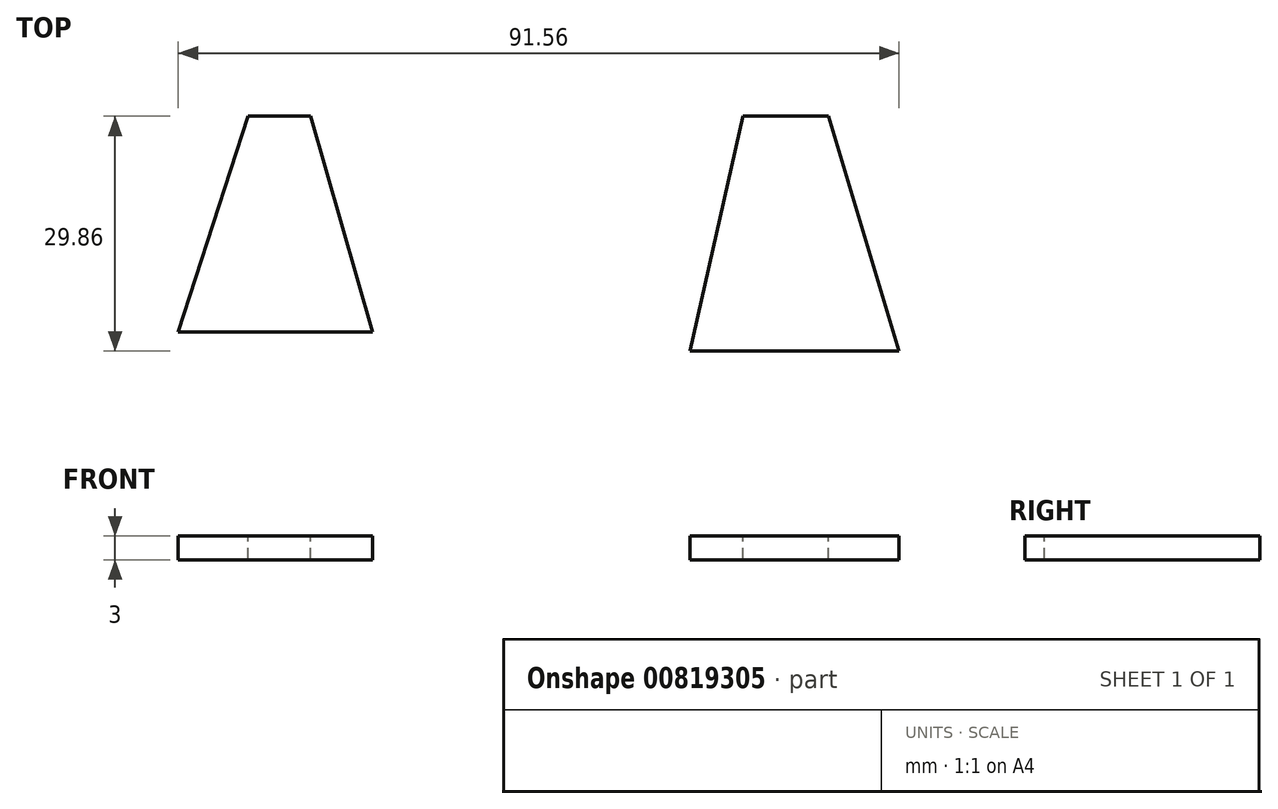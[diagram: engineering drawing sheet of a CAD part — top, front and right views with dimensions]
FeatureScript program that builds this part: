
annotation { "Feature Type Name" : "Feature", "Feature Type Description" : "" }
export const myFeature = defineFeature(function(context is Context, id is Id, definition is map)
    precondition{}
    {
        {
            var Q0;
            Q0=qCreatedBy(makeId("Top.planeOp"),FACE);
            var sketch = newSketch(context, id + "F0", { "sketchPlane" : qUnion([Q0])});
            skLineSegment(sketch, "E0.bottom", {"start": v(0, 0) * mm, "end": v(100, 0) * mm});
            skLineSegment(sketch, "E0.top", {"start": v(0, 150) * mm, "end": v(100, 150) * mm});
            skLineSegment(sketch, "E0.left", {"start": v(0, 0) * mm, "end": v(0, 150) * mm});
            skLineSegment(sketch, "E0.right", {"start": v(100, 0) * mm, "end": v(100, 150) * mm});
            skSolve(sketch);
        }
        {
            var Q0;
            Q0=makeQuery(id+"F0.imprint","IMPRINT",FACE,{"disambiguationData":[TD([[makeQuery(id+"F0.imprint","IMPRINT",EDGE,{"derivedFrom":sQuery(id+"F0.wireOp",EDGE,"E0.bottom")}),1.0]])]});
            var sketch = newSketch(context, id + "F1", { "sketchPlane" : qUnion([Q0])});
            skSolve(sketch);
        }
        {
            var Q0;
            Q0=makeQuery(id+"F1.imprint","IMPRINT",FACE,{"disambiguationData":[TD([[makeQuery(id+"F1.imprint","IMPRINT",EDGE,{"derivedFrom":makeQuery(id+"F0.imprint","IMPRINT",EDGE,{"derivedFrom":sQuery(id+"F0.wireOp",EDGE,"E0.bottom")})}),1.0]])]});
            extrude(context, id + "F2", {"entities" : qUnion([Q0]), "depth" : 3 * mm, "offsetDistance" : 25 * mm});
        }
        {
            var Q0;
            Q0=makeQuery(id+"F2.opExtrude","CAP_FACE",FACE,{"disambiguationData":[OSD([sQuery(id+"F0.wireOp",EDGE,"E0.bottom"),sQuery(id+"F0.wireOp",EDGE,"E0.top"),sQuery(id+"F0.wireOp",EDGE,"E0.left"),sQuery(id+"F0.wireOp",EDGE,"E0.right")])],"isStart":false});
            var sketch = newSketch(context, id + "F3", { "sketchPlane" : qUnion([Q0])});
            skLineSegment(sketch, "E1", {"start": v(0, 150) * mm, "end": v(100, 150) * mm});
            skLineSegment(sketch, "E2", {"start": v(100, 150) * mm, "end": v(38.52, 247.5) * mm});
            skLineSegment(sketch, "E3", {"start": v(38.52, 247.5) * mm, "end": v(0, 150) * mm});
            skSolve(sketch);
        }
        {
            var Q0;
            Q0=makeQuery(id+"F3.imprint","IMPRINT",FACE,{"disambiguationData":[TD([[makeQuery(id+"F3.imprint","IMPRINT",EDGE,{"derivedFrom":sQuery(id+"F3.wireOp",EDGE,"E1")}),1.0]])]});
            extrude(context, id + "F4", {"entities" : qUnion([Q0]), "operationType" : NewBodyOperationType.ADD, "oppositeDirection" : true, "depth" : 3 * mm, "offsetDistance" : 25 * mm});
        }
        {
            var Q0;
            Q0=makeQuery(id+"F4.boolean.opBoolean","MERGE",FACE,{"derivedFrom":[makeQuery(id+"F2.opExtrude","CAP_FACE",FACE,{"disambiguationData":[OSD([sQuery(id+"F0.wireOp",EDGE,"E0.bottom"),sQuery(id+"F0.wireOp",EDGE,"E0.top"),sQuery(id+"F0.wireOp",EDGE,"E0.left"),sQuery(id+"F0.wireOp",EDGE,"E0.right")])],"isStart":false}),makeQuery(id+"F4.opExtrude","CAP_FACE",FACE,{"disambiguationData":[OSD([sQuery(id+"F3.wireOp",EDGE,"E1"),sQuery(id+"F3.wireOp",EDGE,"E2"),sQuery(id+"F3.wireOp",EDGE,"E3")])],"isStart":true})]});
            var sketch = newSketch(context, id + "F5", { "sketchPlane" : qUnion([Q0])});
            skLineSegment(sketch, "E4", {"start": v(8.85, 0) * mm, "end": v(0, -27.4) * mm});
            skLineSegment(sketch, "E5", {"start": v(0, -27.4) * mm, "end": v(24.68, -27.4) * mm});
            skLineSegment(sketch, "E6", {"start": v(24.68, -27.4) * mm, "end": v(16.82, 0) * mm});
            skLineSegment(sketch, "E7", {"start": v(16.82, 0) * mm, "end": v(71.74, 0) * mm});
            skLineSegment(sketch, "E8", {"start": v(71.74, 0) * mm, "end": v(65, -29.86) * mm});
            skLineSegment(sketch, "E9", {"start": v(65, -29.86) * mm, "end": v(91.56, -29.86) * mm});
            skLineSegment(sketch, "E10", {"start": v(91.56, -29.86) * mm, "end": v(82.59, 0) * mm});
            skLineSegment(sketch, "E11", {"start": v(82.59, 0) * mm, "end": v(16.82, 0) * mm});
            skSolve(sketch);
        }
        {
            var Q0;
            {var subQ0=sQuery(id+"F5.wireOp",EDGE,"E4");Q0=makeQuery(id+"F5.imprint","IMPRINT",FACE,{"disambiguationData":[TD([[makeQuery(id+"F5.imprint","IMPRINT",EDGE,{"derivedFrom":subQ0}),1.0]])]});}
            var Q1;
            {var subQ0=sQuery(id+"F5.wireOp",EDGE,"E8");Q1=makeQuery(id+"F5.imprint","IMPRINT",FACE,{"disambiguationData":[TD([[makeQuery(id+"F5.imprint","IMPRINT",EDGE,{"derivedFrom":subQ0}),1.0]])]});}
            extrude(context, id + "F6", {"entities" : qUnion([Q0, Q1]), "operationType" : NewBodyOperationType.ADD, "oppositeDirection" : true, "depth" : 3 * mm, "offsetDistance" : 25 * mm});
        }
        {
            var Q0;
            {var subQ1=makeQuery(id+"F2.opExtrude","CAP_EDGE",EDGE,{"disambiguationData":[OSD([sQuery(id+"F0.wireOp",EDGE,"E0.left")])],"isStart":false});Q0=makeQuery(id+"F5.imprint","IMPRINT",FACE,{"disambiguationData":[TD([[makeQuery(id+"F5.imprint","IMPRINT",EDGE,{"derivedFrom":subQ1}),-1.0]])]});}
            var Q1;
            Q1=makeQuery(id+"FFWewDy7SsHjqFG_1.imprint","IMPRINT",FACE,{"disambiguationData":[TD([[makeQuery(id+"FFWewDy7SsHjqFG_1.imprint","IMPRINT",EDGE,{"derivedFrom":sQuery(id+"FFWewDy7SsHjqFG_1.wireOp",EDGE,"4e26908d-02cd-4f9a-a2f5-5ed4474a62a8.0.startCap")}),-1.0]])]});
            extrude(context, id + "F7", {"entities" : qUnion([Q0, Q1]), "operationType" : NewBodyOperationType.REMOVE, "oppositeDirection" : true, "depth" : 184.78 * mm, "offsetDistance" : 25 * mm});
        }
        {
            var Q0;
            {var subQ1=makeQuery(id+"F2.opExtrude","CAP_EDGE",EDGE,{"disambiguationData":[OSD([sQuery(id+"F0.wireOp",EDGE,"E0.left")])],"isStart":false});Q0=makeQuery(id+"F5.imprint","IMPRINT",FACE,{"disambiguationData":[TD([[makeQuery(id+"F5.imprint","IMPRINT",EDGE,{"derivedFrom":subQ1}),-1.0]])]});}
            var sketch = newSketch(context, id + "F8", { "sketchPlane" : qUnion([Q0])});
            skLineSegment(sketch, "E12", {"start": v(74.25, 76.49) * mm, "end": v(74.25, 31.1) * mm});
            skLineSegment(sketch, "E13", {"start": v(74.25, 31.1) * mm, "end": v(74.25, 76.49) * mm});
            skSolve(sketch);
        }
        {
            var Q0;
            {var subQ1=makeQuery(id+"F2.opExtrude","CAP_EDGE",EDGE,{"disambiguationData":[OSD([sQuery(id+"F0.wireOp",EDGE,"E0.left")])],"isStart":false});Q0=makeQuery(id+"F5.imprint","IMPRINT",FACE,{"disambiguationData":[TD([[makeQuery(id+"F5.imprint","IMPRINT",EDGE,{"derivedFrom":subQ1}),-1.0]])]});}
            var sketch = newSketch(context, id + "F9", { "sketchPlane" : qUnion([Q0])});
            skLineSegment(sketch, "E14.JWF.JWF", {"start": v(74.25, 31.1) * mm, "end": v(74.25, 76.49) * mm, "construction": true});
            skArc(sketch, "E14.0.startCap", {"start": v(76.75, 31.1) * mm, "mid": v(74.25, 28.6) * mm, "end": v(71.75, 31.1) * mm});
            skArc(sketch, "E14.0.endCap", {"start": v(71.75, 76.49) * mm, "mid": v(74.25, 78.99) * mm, "end": v(76.75, 76.49) * mm});
            skLineSegment(sketch, "E14.0.left", {"start": v(71.75, 31.1) * mm, "end": v(71.75, 76.49) * mm});
            skLineSegment(sketch, "E14.0.right", {"start": v(76.75, 31.1) * mm, "end": v(76.75, 76.49) * mm});
            skSolve(sketch);
        }
        {
            var Q0;
            Q0=makeQuery(id+"F3.imprint","IMPRINT",FACE,{"disambiguationData":[TD([[makeQuery(id+"F3.imprint","IMPRINT",EDGE,{"derivedFrom":sQuery(id+"F3.wireOp",EDGE,"E1")}),-1.0]])]});
            extrude(context, id + "F10", {"entities" : qUnion([Q0]), "operationType" : NewBodyOperationType.REMOVE, "oppositeDirection" : true, "depth" : 25 * mm, "offsetDistance" : 25 * mm});
        }
        {
            var Q0;
            Q0=makeQuery(id+"F9.imprint","IMPRINT",FACE,{"disambiguationData":[TD([[makeQuery(id+"F9.imprint","IMPRINT",EDGE,{"derivedFrom":sQuery(id+"F9.wireOp",EDGE,"E14.0.startCap")}),-1.0]])]});
            extrude(context, id + "F11", {"entities" : qUnion([Q0]), "operationType" : NewBodyOperationType.REMOVE, "oppositeDirection" : true, "depth" : 170 * mm, "offsetDistance" : 25 * mm});
        }
    });
